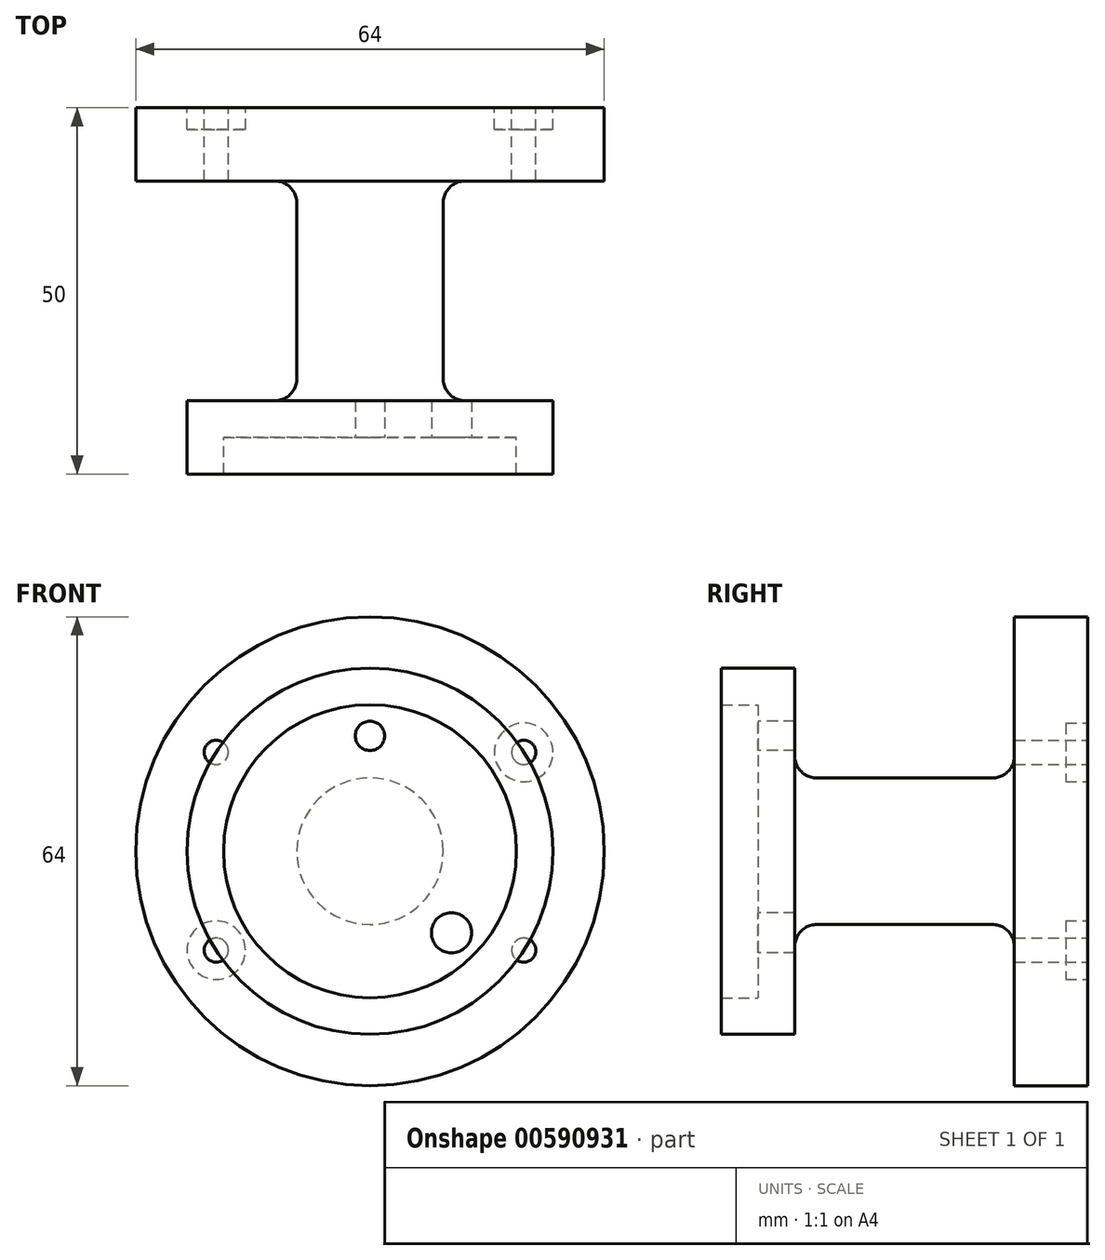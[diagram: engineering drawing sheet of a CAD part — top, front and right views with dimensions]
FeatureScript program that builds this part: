
annotation { "Feature Type Name" : "Feature", "Feature Type Description" : "" }
export const myFeature = defineFeature(function(context is Context, id is Id, definition is map)
    precondition{}
    {
        {
            var Q0;
            Q0=qCreatedBy(makeId("Top.planeOp"),FACE);
            var sketch = newSketch(context, id + "F0", { "sketchPlane" : qUnion([Q0])});
            skLineSegment(sketch, "E0", {"start": v(-20, 0) * mm, "end": v(-25, 0) * mm});
            skLineSegment(sketch, "E1", {"start": v(-25, 0) * mm, "end": v(-25, 10) * mm});
            skLineSegment(sketch, "E2", {"start": v(-25, 10) * mm, "end": v(-13, 10) * mm});
            skLineSegment(sketch, "E3", {"start": v(-10, 13) * mm, "end": v(-10, 37) * mm});
            skLineSegment(sketch, "E4", {"start": v(-13, 40) * mm, "end": v(-32, 40) * mm});
            skLineSegment(sketch, "E5", {"start": v(-32, 40) * mm, "end": v(-32, 50) * mm});
            skLineSegment(sketch, "E6", {"start": v(-32, 50) * mm, "end": v(0, 50) * mm});
            skLineSegment(sketch, "E7", {"start": v(0, 50) * mm, "end": v(0, 5) * mm});
            skLineSegment(sketch, "E8", {"start": v(0, 5) * mm, "end": v(-20, 5) * mm});
            skLineSegment(sketch, "E9", {"start": v(-20, 5) * mm, "end": v(-20, 0) * mm});
            skPoint(sketch, "E10.visualSharp", {"position": v(-10, 40) * mm});
            skArc(sketch, "E10.filletArc", {"start": v(-10, 37) * mm, "mid": v(-10.88, 39.12) * mm, "end": v(-13, 40) * mm});
            skPoint(sketch, "E11.visualSharp", {"position": v(-10, 10) * mm});
            skArc(sketch, "E11.filletArc", {"start": v(-13, 10) * mm, "mid": v(-10.88, 10.88) * mm, "end": v(-10, 13) * mm});
            skSolve(sketch);
        }
        {
            var Q0;
            Q0=makeQuery(id+"F0.imprint","IMPRINT",FACE,{"disambiguationData":[TD([[makeQuery(id+"F0.imprint","IMPRINT",EDGE,{"derivedFrom":sQuery(id+"F0.wireOp",EDGE,"E0")}),-1.0]])]});
            var Q1;
            Q1=sQuery(id+"F0.wireOp",EDGE,"E7");
            revolve(context, id + "F1", {"entities" : qUnion([Q0]), "axis" : qUnion([Q1]), "revolveType" : RevolveType.FULL});
        }
        {
            var Q0;
            Q0=makeQuery(id+"F1.opRevolve","SWEPT_FACE",FACE,{"disambiguationData":[OSD([sQuery(id+"F0.wireOp",EDGE,"E6")])]});
            var sketch = newSketch(context, id + "F2", { "sketchPlane" : qUnion([Q0])});
            skPoint(sketch, "E12", {"position": v(21, -13.5) * mm});
            skPoint(sketch, "E13", {"position": v(21, 13.5) * mm});
            skPoint(sketch, "E14", {"position": v(-21, 13.5) * mm});
            skPoint(sketch, "E15", {"position": v(-21, -13.5) * mm});
            skCircle(sketch, "E16", {"center": v(21, -13.5) * mm, "radius": 4 * mm});
            skCircle(sketch, "E17", {"center": v(-21, 13.5) * mm, "radius": 4 * mm});
            skSolve(sketch);
        }
        {
            var Q0;
            Q0=sQuery(id+"F2.wireOp",VERTEX,"E12");
            var Q1;
            Q1=sQuery(id+"F2.wireOp",VERTEX,"E13");
            var Q2;
            Q2=sQuery(id+"F2.wireOp",VERTEX,"E14");
            var Q3;
            Q3=sQuery(id+"F2.wireOp",VERTEX,"E15");
            var Q4;
            Q4=makeQuery(id+"F1.opRevolve","SWEPT_BODY",BODY,{"disambiguationData":[OSD([sQuery(id+"F0.wireOp",EDGE,"E0"),sQuery(id+"F0.wireOp",EDGE,"E1"),sQuery(id+"F0.wireOp",EDGE,"E2"),sQuery(id+"F0.wireOp",EDGE,"E3"),sQuery(id+"F0.wireOp",EDGE,"E4"),sQuery(id+"F0.wireOp",EDGE,"E5"),sQuery(id+"F0.wireOp",EDGE,"E6"),sQuery(id+"F0.wireOp",EDGE,"E7"),sQuery(id+"F0.wireOp",EDGE,"E8"),sQuery(id+"F0.wireOp",EDGE,"E9"),sQuery(id+"F0.wireOp",EDGE,"E10.filletArc"),sQuery(id+"F0.wireOp",EDGE,"E11.filletArc")])]});
            hole(context, id + "F3", {"style" : HoleStyle.SIMPLE, "endStyle" : HoleEndStyle.BLIND, "standardTappedOrClearance" : lookupTablePath({ "standard" : "ISO", "engagement" : "75%", "pitch" : "0.7 mm", "size" : "M4", "type" : "Tapped" }), "standardBlindInLast" : lookupTablePath({ "standard" : "ISO", "engagement" : "75%", "pitch" : "0.7 mm", "size" : "M4", "type" : "Tapped" }), "holeDiameter" : 3.3 * mm, "majorDiameter" : 4 * mm, "showTappedDepth" : true, "holeDepth" : 14.1 * mm, "isTappedThrough" : true, "tappedDepth" : 12 * mm, "tapClearance" : 3, "locations" : qUnion([Q0, Q1, Q2, Q3]), "scope" : qUnion([Q4])});
        }
        {
            var Q0;
            Q0 = qSketchRegion(id + "F2", true);
            extrude(context, id + "F4", {"entities" : qUnion([Q0]), "operationType" : NewBodyOperationType.REMOVE, "oppositeDirection" : true, "depth" : 3 * mm, "offsetDistance" : 25 * mm});
        }
        {
            var Q0;
            Q0=makeQuery(id+"F1.opRevolve","SWEPT_FACE",FACE,{"disambiguationData":[OSD([sQuery(id+"F0.wireOp",EDGE,"E8")])]});
            var sketch = newSketch(context, id + "F5", { "sketchPlane" : qUnion([Q0])});
            skLineSegment(sketch, "E18", {"start": v(0, 0) * mm, "end": v(14.14, -14.14) * mm, "construction": true});
            skCircle(sketch, "E19", {"center": v(0, 0) * mm, "radius": 15.75 * mm, "construction": true});
            skPoint(sketch, "E20", {"position": v(11.14, -11.14) * mm});
            skCircle(sketch, "E21", {"center": v(11.14, -11.14) * mm, "radius": 2.75 * mm});
            skSolve(sketch);
        }
        {
            var Q0;
            Q0 = qSketchRegion(id + "F5", true);
            extrude(context, id + "F6", {"entities" : qUnion([Q0]), "operationType" : NewBodyOperationType.REMOVE, "oppositeDirection" : true, "depth" : 25 * mm, "offsetDistance" : 25 * mm});
        }
        {
            var Q0;
            Q0=qCreatedBy(makeId("Top.planeOp"),FACE);
            var sketch = newSketch(context, id + "F7", { "sketchPlane" : qUnion([Q0])});
            skLineSegment(sketch, "E22", {"start": v(0, 54.13) * mm, "end": v(0, -5.63) * mm, "construction": true});
            skSolve(sketch);
        }
        {
            var Q0;
            Q0=makeQuery(id+"F1.opRevolve","SWEPT_FACE",FACE,{"disambiguationData":[OSD([sQuery(id+"F0.wireOp",EDGE,"E8")])]});
            var sketch = newSketch(context, id + "F8", { "sketchPlane" : qUnion([Q0])});
            skPoint(sketch, "E23", {"position": v(0, 15.75) * mm});
            skCircle(sketch, "E24", {"center": v(0, 15.75) * mm, "radius": 2 * mm});
            skSolve(sketch);
        }
        {
            var Q0;
            Q0 = qSketchRegion(id + "F8", true);
            extrude(context, id + "F9", {"entities" : qUnion([Q0]), "operationType" : NewBodyOperationType.REMOVE, "oppositeDirection" : true, "depth" : 25 * mm, "offsetDistance" : 25 * mm});
        }
    });
